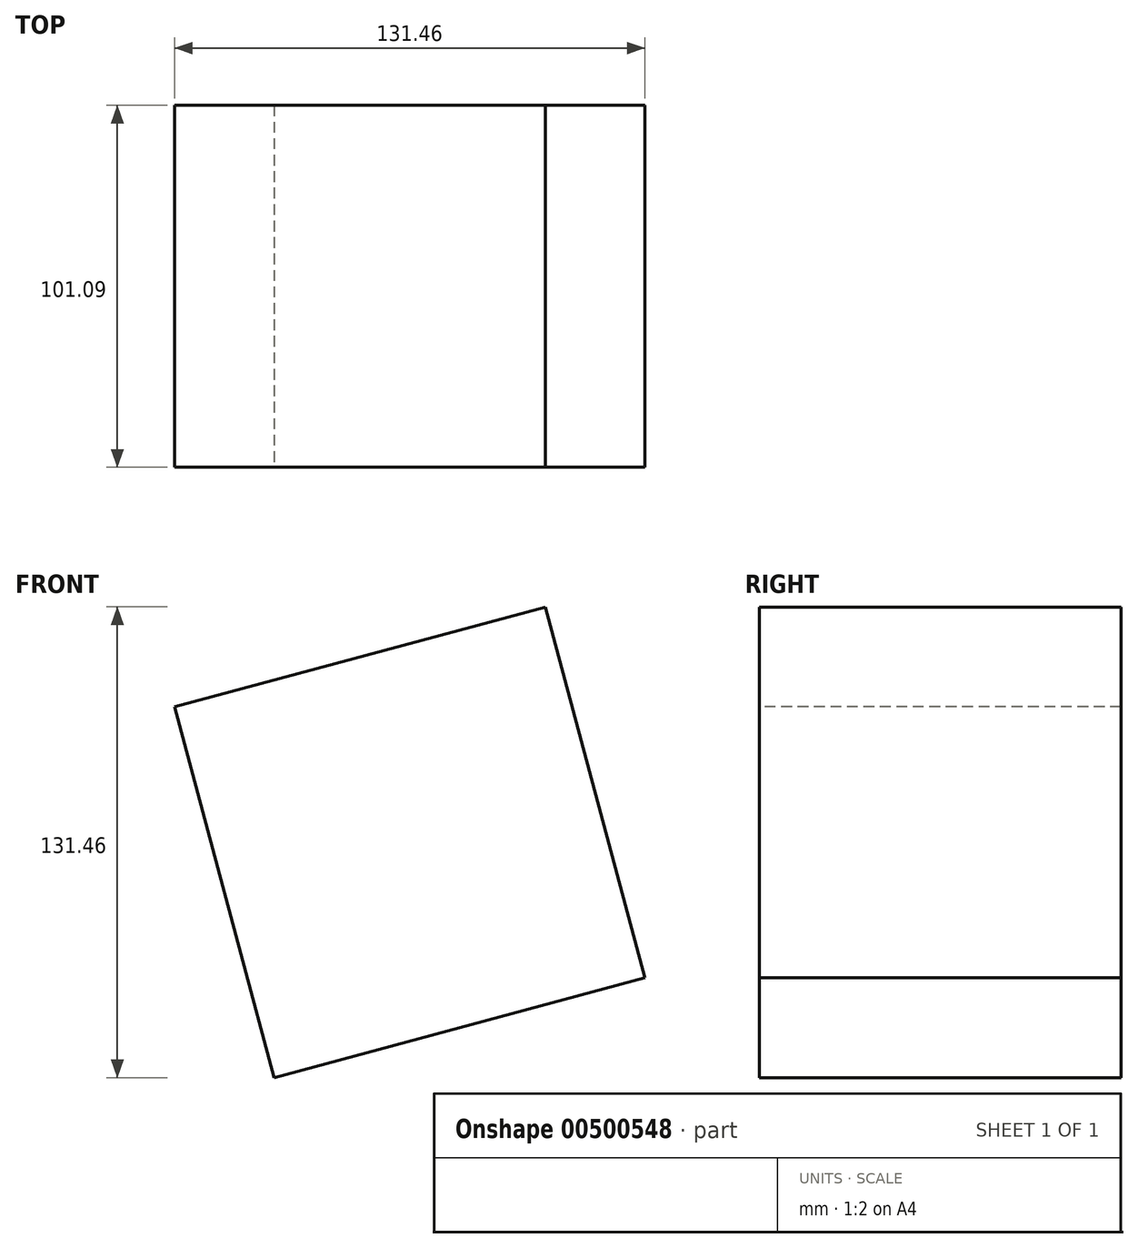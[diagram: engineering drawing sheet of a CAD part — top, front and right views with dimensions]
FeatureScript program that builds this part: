
annotation { "Feature Type Name" : "Feature", "Feature Type Description" : "" }
export const myFeature = defineFeature(function(context is Context, id is Id, definition is map)
    precondition{}
    {
        {
            var Q0;
            Q0=qCreatedBy(makeId("Front.planeOp"),FACE);
            var sketch = newSketch(context, id + "F0", { "sketchPlane" : qUnion([Q0])});
            skCircle(sketch, "E0.cCircle", {"center": v(0, 0) * mm, "radius": 75.87 * mm, "construction": true});
            skLineSegment(sketch, "E0.0", {"start": v(37.9, 65.73) * mm, "end": v(65.73, -37.9) * mm});
            skLineSegment(sketch, "E0.1", {"start": v(65.73, -37.9) * mm, "end": v(-37.9, -65.73) * mm});
            skLineSegment(sketch, "E0.2", {"start": v(-37.9, -65.73) * mm, "end": v(-65.73, 37.9) * mm});
            skLineSegment(sketch, "E0.3", {"start": v(-65.73, 37.9) * mm, "end": v(37.9, 65.73) * mm});
            skSolve(sketch);
        }
        {
            var Q0;
            Q0=makeQuery(id+"F0.imprint","IMPRINT",FACE,{"disambiguationData":[TD([[makeQuery(id+"F0.imprint","IMPRINT",EDGE,{"derivedFrom":sQuery(id+"F0.wireOp",EDGE,"E0.0")}),-1.0]])]});
            extrude(context, id + "F1", {"entities" : qUnion([Q0]), "oppositeDirection" : true, "depth" : 101.1 * mm});
        }
    });
